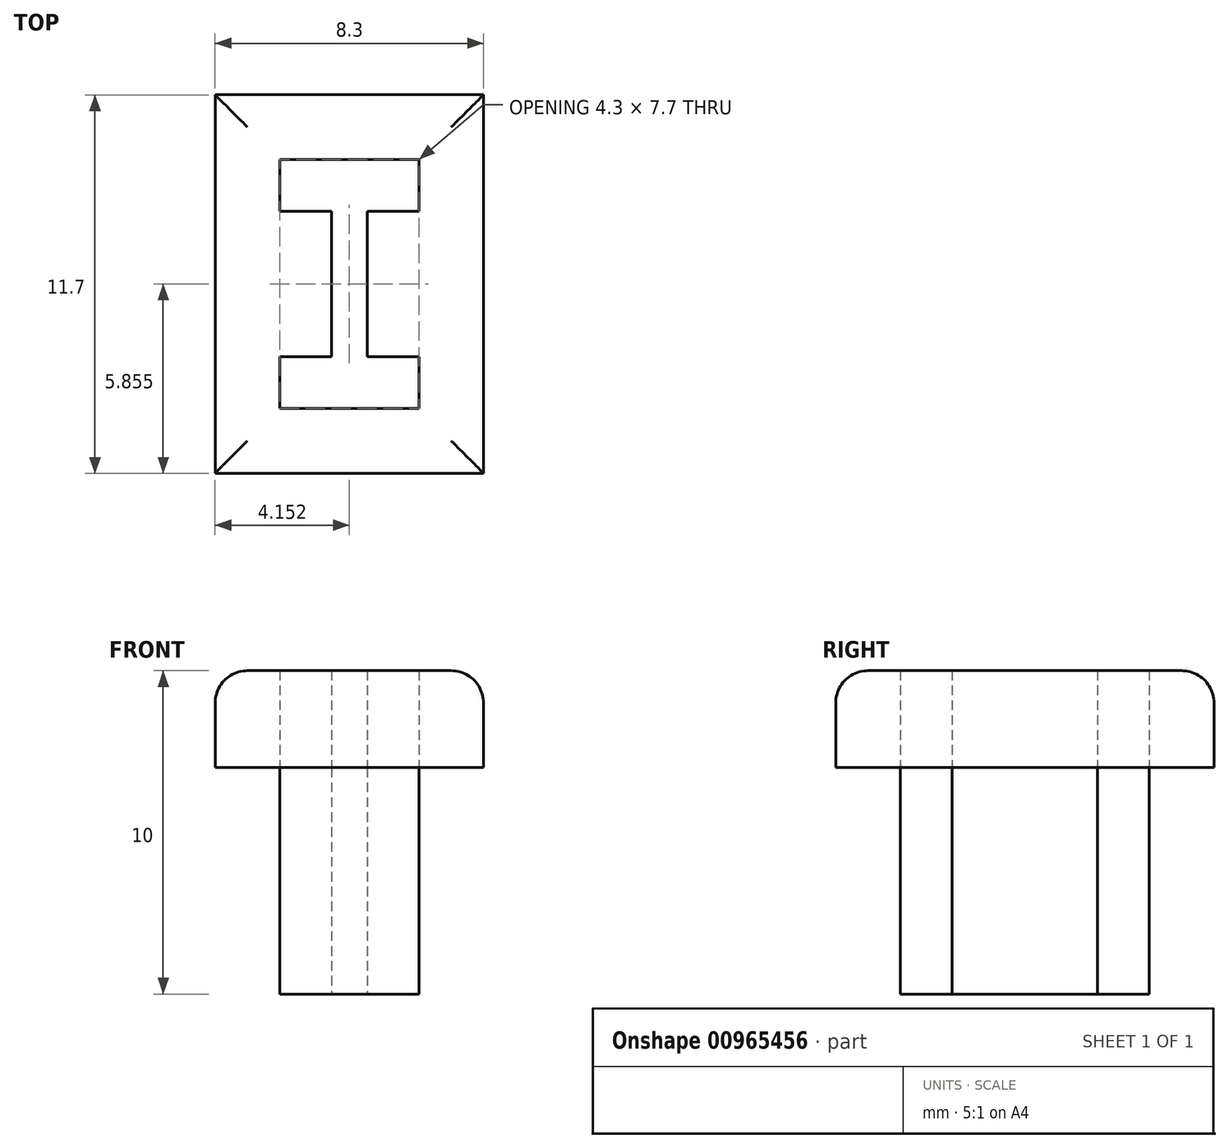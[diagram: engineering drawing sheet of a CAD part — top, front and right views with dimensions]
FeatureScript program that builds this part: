
annotation { "Feature Type Name" : "Feature", "Feature Type Description" : "" }
export const myFeature = defineFeature(function(context is Context, id is Id, definition is map)
    precondition{}
    {
        {
            var Q0;
            Q0=qCreatedBy(makeId("Top.planeOp"),FACE);
            var sketch = newSketch(context, id + "F0", { "sketchPlane" : qUnion([Q0])});
            skLineSegment(sketch, "E0", {"start": v(-40.75, -13.64) * mm, "end": v(-40.75, -18.14) * mm});
            skLineSegment(sketch, "E1", {"start": v(-40.75, -18.14) * mm, "end": v(-42.35, -18.14) * mm});
            skLineSegment(sketch, "E2", {"start": v(-42.35, -18.14) * mm, "end": v(-42.35, -19.74) * mm});
            skLineSegment(sketch, "E3", {"start": v(-42.35, -19.74) * mm, "end": v(-38.05, -19.74) * mm});
            skLineSegment(sketch, "E4", {"start": v(-38.05, -19.74) * mm, "end": v(-38.05, -18.14) * mm});
            skLineSegment(sketch, "E5", {"start": v(-38.05, -18.14) * mm, "end": v(-39.65, -18.14) * mm});
            skLineSegment(sketch, "E6", {"start": v(-39.65, -18.14) * mm, "end": v(-39.65, -13.64) * mm});
            skLineSegment(sketch, "E7", {"start": v(-40.75, -13.64) * mm, "end": v(-42.35, -13.64) * mm});
            skLineSegment(sketch, "E8", {"start": v(-42.35, -13.64) * mm, "end": v(-42.35, -12.04) * mm});
            skLineSegment(sketch, "E9", {"start": v(-42.35, -12.04) * mm, "end": v(-38.05, -12.04) * mm});
            skLineSegment(sketch, "E10", {"start": v(-38.05, -12.04) * mm, "end": v(-38.05, -13.64) * mm});
            skLineSegment(sketch, "E11", {"start": v(-38.05, -13.64) * mm, "end": v(-39.65, -13.64) * mm});
            skSolve(sketch);
        }
        {
            var Q0;
            Q0=makeQuery(id+"F0.imprint","IMPRINT",FACE,{"disambiguationData":[TD([[makeQuery(id+"F0.imprint","IMPRINT",EDGE,{"derivedFrom":sQuery(id+"F0.wireOp",EDGE,"E0")}),1.0]])]});
            extrude(context, id + "F1", {"entities" : qUnion([Q0]), "depth" : 7 * mm, "offsetDistance" : 25 * mm});
        }
        {
            var Q0;
            Q0=makeQuery(id+"F1.opExtrude","CAP_FACE",FACE,{"disambiguationData":[OSD([sQuery(id+"F0.wireOp",EDGE,"E0"),sQuery(id+"F0.wireOp",EDGE,"E1"),sQuery(id+"F0.wireOp",EDGE,"E2"),sQuery(id+"F0.wireOp",EDGE,"E3"),sQuery(id+"F0.wireOp",EDGE,"E4"),sQuery(id+"F0.wireOp",EDGE,"E5"),sQuery(id+"F0.wireOp",EDGE,"E6"),sQuery(id+"F0.wireOp",EDGE,"E7"),sQuery(id+"F0.wireOp",EDGE,"E8"),sQuery(id+"F0.wireOp",EDGE,"E9"),sQuery(id+"F0.wireOp",EDGE,"E10"),sQuery(id+"F0.wireOp",EDGE,"E11")])],"isStart":false});
            var sketch = newSketch(context, id + "F2", { "sketchPlane" : qUnion([Q0])});
            skLineSegment(sketch, "E12.0", {"start": v(-44.35, -18.64) * mm, "end": v(-44.35, -10.04) * mm});
            skLineSegment(sketch, "E12.1", {"start": v(-36.05, -10.04) * mm, "end": v(-36.05, -13.14) * mm});
            skLineSegment(sketch, "E12.2", {"start": v(-36.05, -21.74) * mm, "end": v(-36.05, -13.14) * mm});
            skLineSegment(sketch, "E12.3", {"start": v(-44.35, -10.04) * mm, "end": v(-36.05, -10.04) * mm});
            skLineSegment(sketch, "E12.4", {"start": v(-44.35, -21.74) * mm, "end": v(-36.05, -21.74) * mm});
            skLineSegment(sketch, "E12.5", {"start": v(-44.35, -18.64) * mm, "end": v(-44.35, -21.74) * mm});
            skSolve(sketch);
        }
        {
            var Q0;
            Q0=makeQuery(id+"F2.imprint","IMPRINT",FACE,{"disambiguationData":[TD([[makeQuery(id+"F2.imprint","IMPRINT",EDGE,{"derivedFrom":sQuery(id+"F2.wireOp",EDGE,"E12.0")}),-1.0]])]});
            extrude(context, id + "F3", {"entities" : qUnion([Q0]), "depth" : 3 * mm, "offsetDistance" : 25 * mm});
        }
        {
            var Q0;
            Q0=makeQuery(id+"F1.opExtrude","CAP_FACE",FACE,{"disambiguationData":[OSD([sQuery(id+"F0.wireOp",EDGE,"E0"),sQuery(id+"F0.wireOp",EDGE,"E1"),sQuery(id+"F0.wireOp",EDGE,"E2"),sQuery(id+"F0.wireOp",EDGE,"E3"),sQuery(id+"F0.wireOp",EDGE,"E4"),sQuery(id+"F0.wireOp",EDGE,"E5"),sQuery(id+"F0.wireOp",EDGE,"E6"),sQuery(id+"F0.wireOp",EDGE,"E7"),sQuery(id+"F0.wireOp",EDGE,"E8"),sQuery(id+"F0.wireOp",EDGE,"E9"),sQuery(id+"F0.wireOp",EDGE,"E10"),sQuery(id+"F0.wireOp",EDGE,"E11")])],"isStart":false});
            extrude(context, id + "F4", {"entities" : qUnion([Q0]), "depth" : 3 * mm, "offsetDistance" : 25 * mm});
        }
        {
            var Q0;
            Q0=makeQuery(id+"F3.opExtrude","CAP_EDGE",EDGE,{"disambiguationData":[OSD([sQuery(id+"F2.wireOp",EDGE,"E12.3")])],"isStart":false});
            var Q1;
            Q1=makeQuery(id+"F3.opExtrude","CAP_EDGE",EDGE,{"disambiguationData":[OSD([sQuery(id+"F2.wireOp",EDGE,"E12.0"),sQuery(id+"F2.wireOp",EDGE,"E12.5")])],"isStart":false});
            var Q2;
            Q2=makeQuery(id+"F3.opExtrude","CAP_EDGE",EDGE,{"disambiguationData":[OSD([sQuery(id+"F2.wireOp",EDGE,"E12.4")])],"isStart":false});
            var Q3;
            Q3=makeQuery(id+"F3.opExtrude","CAP_EDGE",EDGE,{"disambiguationData":[OSD([sQuery(id+"F2.wireOp",EDGE,"E12.1"),sQuery(id+"F2.wireOp",EDGE,"E12.2")])],"isStart":false});
            fillet(context, id + "F5", {"entities" : qUnion([Q0, Q1, Q2, Q3]), "tangentPropagation" : true, "radius" : 1 * mm, "defaultsChanged" : true, "vertexSettings" : [], "allowEdgeOverflow" : false});
        }
    });
